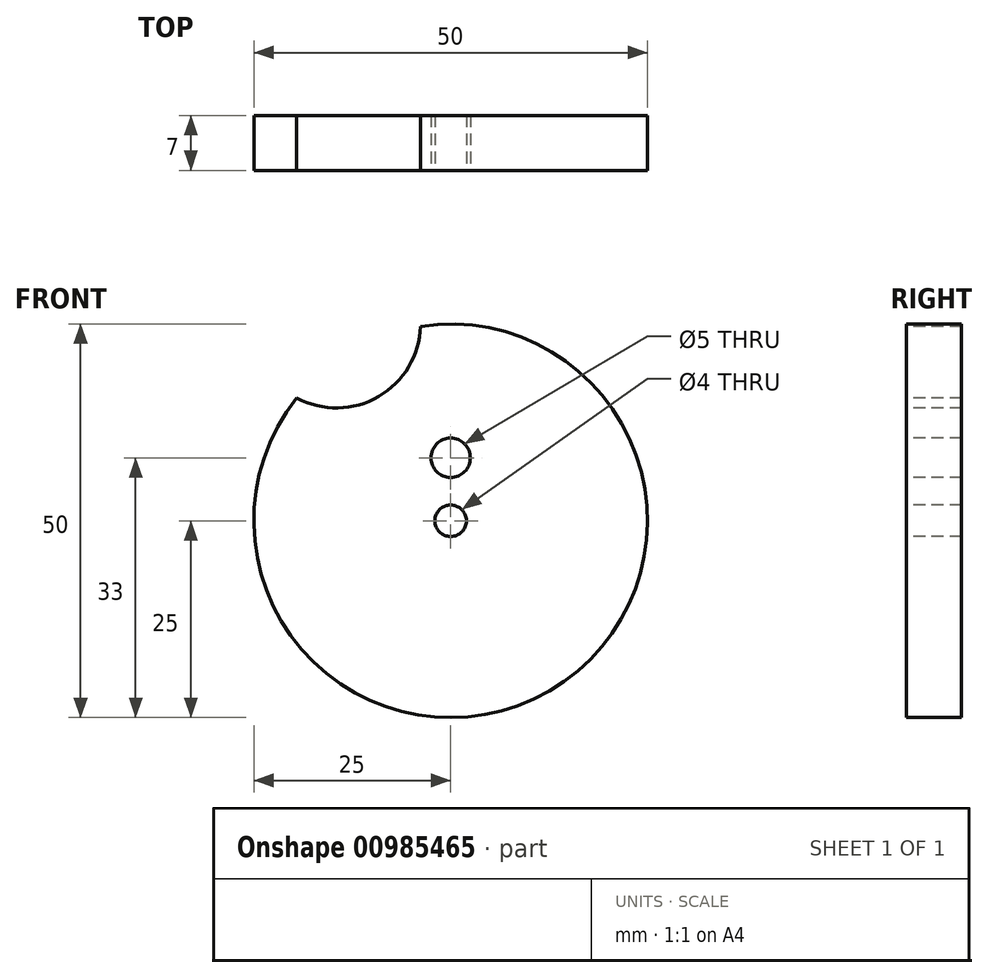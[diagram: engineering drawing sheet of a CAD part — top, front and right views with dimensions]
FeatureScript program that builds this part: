
annotation { "Feature Type Name" : "Feature", "Feature Type Description" : "" }
export const myFeature = defineFeature(function(context is Context, id is Id, definition is map)
    precondition{}
    {
        {
            var Q0;
            Q0=qCreatedBy(makeId("Front.planeOp"),FACE);
            var sketch = newSketch(context, id + "F0", { "sketchPlane" : qUnion([Q0])});
            skCircle(sketch, "E0", {"center": v(0, 0) * mm, "radius": 25 * mm});
            skSolve(sketch);
        }
        {
            var Q0;
            Q0=makeQuery(id+"F0.imprint","IMPRINT",FACE,{"disambiguationData":[TD([[makeQuery(id+"F0.imprint","IMPRINT",EDGE,{"derivedFrom":sQuery(id+"F0.wireOp",EDGE,"E0")}),1.0]])]});
            extrude(context, id + "F1", {"entities" : qUnion([Q0]), "depth" : 7 * mm, "offsetDistance" : 25 * mm});
        }
        {
            var Q0;
            Q0=makeQuery(id+"F1.opExtrude","CAP_FACE",FACE,{"disambiguationData":[OSD([sQuery(id+"F0.wireOp",EDGE,"E0")])],"isStart":false});
            var sketch = newSketch(context, id + "F2", { "sketchPlane" : qUnion([Q0])});
            skCircle(sketch, "E1", {"center": v(0, 25) * mm, "radius": 2.5 * mm});
            skCircle(sketch, "E2", {"center": v(-14.5, 25) * mm, "radius": 10.67 * mm});
            skCircle(sketch, "E3", {"center": v(0, 8) * mm, "radius": 2.5 * mm});
            skLineSegment(sketch, "E4", {"start": v(2.5, 8) * mm, "end": v(2.5, 25) * mm});
            skLineSegment(sketch, "E5", {"start": v(-2.5, 25) * mm, "end": v(-2.5, 8) * mm});
            skSolve(sketch);
        }
        {
            var Q0;
            {var subQ0=sQuery(id+"F2.wireOp",EDGE,"E2");var subQ1=makeQuery(id+"F1.opExtrude","CAP_EDGE",EDGE,{"disambiguationData":[OSD([sQuery(id+"F0.wireOp",EDGE,"E0")])],"isStart":false});var subQ2=makeQuery(id+"F2.imprint","INTERSECT",VERTEX,{"disambiguationData":[OD(0.0)],"derivedFrom":[subQ1,subQ0]});Q0=makeQuery(id+"F2.imprint","IMPRINT",FACE,{"disambiguationData":[TD([[makeQuery(id+"F2.imprint","IMPRINT",EDGE,{"disambiguationData":[TD([[subQ2,-1.0]])],"derivedFrom":subQ0}),1.0]])]});}
            var Q1;
            {var subQ0=sQuery(id+"F2.wireOp",EDGE,"E2");var subQ1=makeQuery(id+"F1.opExtrude","CAP_EDGE",EDGE,{"disambiguationData":[OSD([sQuery(id+"F0.wireOp",EDGE,"E0")])],"isStart":false});var subQ2=makeQuery(id+"F2.imprint","INTERSECT",VERTEX,{"disambiguationData":[OD(0.0)],"derivedFrom":[subQ1,subQ0]});Q1=makeQuery(id+"F2.imprint","IMPRINT",FACE,{"disambiguationData":[TD([[makeQuery(id+"F2.imprint","IMPRINT",EDGE,{"disambiguationData":[TD([[subQ2,1.0]])],"derivedFrom":subQ0}),1.0]])]});}
            var Q2;
            {var subQ0=sQuery(id+"F2.wireOp",EDGE,"E1");var subQ1=makeQuery(id+"F2.imprint","INTERSECT",VERTEX,{"derivedFrom":[subQ0,sQuery(id+"F2.wireOp",EDGE,"E4")]});Q2=makeQuery(id+"F2.imprint","IMPRINT",FACE,{"disambiguationData":[TD([[makeQuery(id+"F2.imprint","IMPRINT",EDGE,{"disambiguationData":[TD([[subQ1,-1.0]])],"derivedFrom":subQ0}),1.0]])]});}
            var Q3;
            {var subQ0=sQuery(id+"F2.wireOp",EDGE,"E1");var subQ1=makeQuery(id+"F1.opExtrude","CAP_EDGE",EDGE,{"disambiguationData":[OSD([sQuery(id+"F0.wireOp",EDGE,"E0")])],"isStart":false});var subQ2=makeQuery(id+"F2.imprint","INTERSECT",VERTEX,{"disambiguationData":[OD(0.0)],"derivedFrom":[subQ1,subQ0]});Q3=makeQuery(id+"F2.imprint","IMPRINT",FACE,{"disambiguationData":[TD([[makeQuery(id+"F2.imprint","IMPRINT",EDGE,{"disambiguationData":[TD([[subQ2,-1.0]])],"derivedFrom":subQ0}),1.0]])]});}
            var Q4;
            {var subQ3=makeQuery(id+"F1.opExtrude","CAP_EDGE",EDGE,{"disambiguationData":[OSD([sQuery(id+"F0.wireOp",EDGE,"E0")])],"isStart":false});var subQ8=sQuery(id+"F2.wireOp",EDGE,"E1");var subQ9=makeQuery(id+"F2.imprint","INTERSECT",VERTEX,{"disambiguationData":[OD(0.0)],"derivedFrom":[subQ3,subQ8]});Q4=makeQuery(id+"F2.imprint","IMPRINT",FACE,{"disambiguationData":[TD([[makeQuery(id+"F2.imprint","IMPRINT",EDGE,{"disambiguationData":[TD([[subQ9,-1.0]])],"derivedFrom":subQ8}),-1.0]])]});}
            var Q5;
            {var subQ0=sQuery(id+"F2.wireOp",EDGE,"E3");var subQ1=makeQuery(id+"F2.imprint","INTERSECT",VERTEX,{"derivedFrom":[subQ0,sQuery(id+"F2.wireOp",EDGE,"E4")]});Q5=makeQuery(id+"F2.imprint","IMPRINT",FACE,{"disambiguationData":[TD([[makeQuery(id+"F2.imprint","IMPRINT",EDGE,{"disambiguationData":[TD([[subQ1,-1.0]])],"derivedFrom":subQ0}),1.0]])]});}
            extrude(context, id + "F3", {"entities" : qUnion([Q0, Q1, Q2, Q3, Q4, Q5]), "operationType" : NewBodyOperationType.REMOVE, "oppositeDirection" : true, "depth" : 13.3 * mm, "offsetDistance" : 25 * mm});
        }
        {
            var Q0;
            {var subQ3=makeQuery(id+"F1.opExtrude","CAP_EDGE",EDGE,{"disambiguationData":[OSD([sQuery(id+"F0.wireOp",EDGE,"E0")])],"isStart":false});var subQ8=sQuery(id+"F2.wireOp",EDGE,"E2");var subQ9=makeQuery(id+"F2.imprint","INTERSECT",VERTEX,{"disambiguationData":[OD(0.0)],"derivedFrom":[subQ3,subQ8]});Q0=makeQuery(id+"F2.imprint","IMPRINT",FACE,{"disambiguationData":[TD([[makeQuery(id+"F2.imprint","IMPRINT",EDGE,{"disambiguationData":[TD([[subQ9,-1.0]])],"derivedFrom":subQ8}),-1.0]])]});}
            var sketch = newSketch(context, id + "F4", { "sketchPlane" : qUnion([Q0])});
            skCircle(sketch, "E6", {"center": v(0, 0) * mm, "radius": 2 * mm});
            skSolve(sketch);
        }
        {
            var Q0;
            Q0 = qSketchRegion(id + "F4", true);
            extrude(context, id + "F5", {"entities" : qUnion([Q0]), "operationType" : NewBodyOperationType.REMOVE, "oppositeDirection" : true, "depth" : 25 * mm, "offsetDistance" : 25 * mm});
        }
    });
